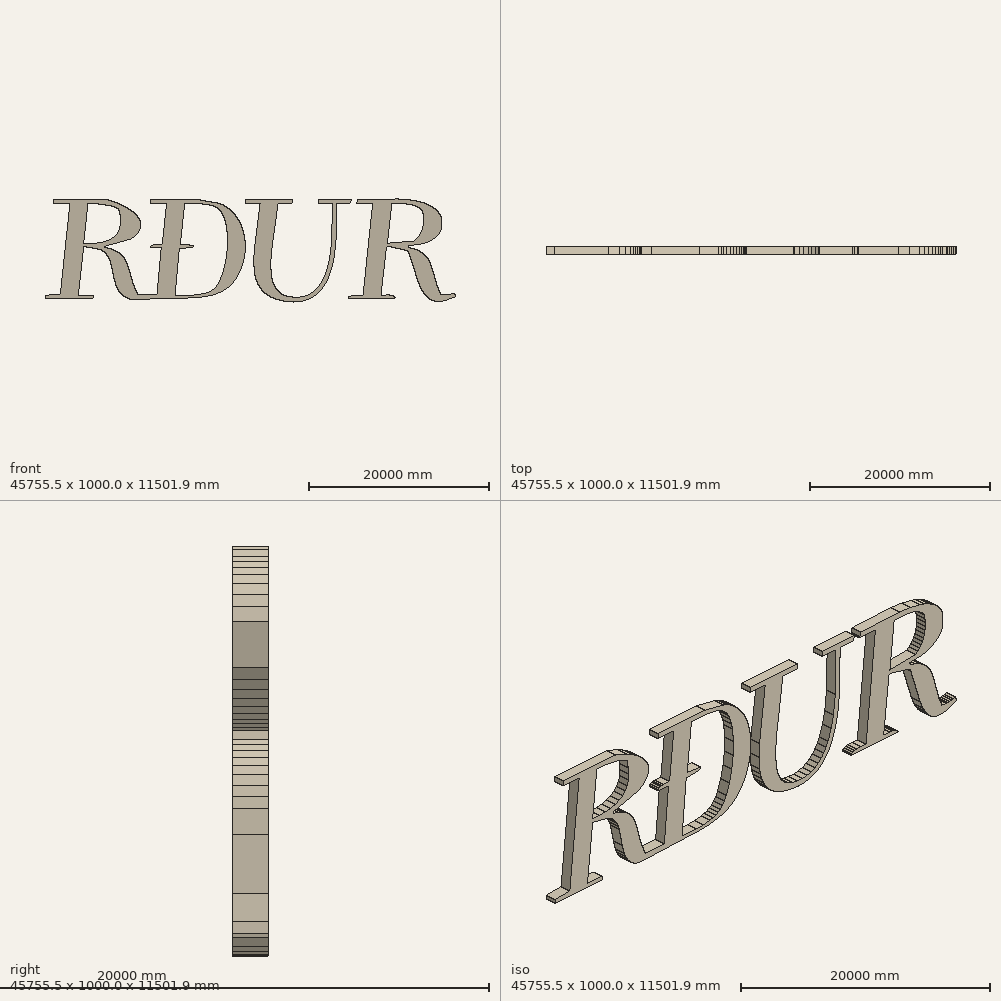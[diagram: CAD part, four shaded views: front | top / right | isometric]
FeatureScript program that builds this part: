
annotation { "Feature Type Name" : "Feature", "Feature Type Description" : "" }
export const myFeature = defineFeature(function(context is Context, id is Id, definition is map)
    precondition{}
    {
        {
            var Q0;
            Q0=qCreatedBy(makeId("Front.planeOp"),FACE);
            var sketch = newSketch(context, id + "F0", { "sketchPlane" : qUnion([Q0])});
            skPoint(sketch, "E0.0", {"position": v(4657, 1520.6) * mm});
            skPoint(sketch, "E1.0", {"position": v(4445.34, -322.18) * mm});
            skPoint(sketch, "E2.0", {"position": v(4195.1, -1476.1) * mm});
            skPoint(sketch, "E3.0", {"position": v(3835.48, -2522.07) * mm});
            skPoint(sketch, "E4.0", {"position": v(4716.46, 5621.12) * mm});
            skPoint(sketch, "E5.0", {"position": v(3175.32, 5621.43) * mm});
            skPoint(sketch, "E6.0", {"position": v(3175.32, 6095.06) * mm});
            skPoint(sketch, "E7.0", {"position": v(6849.4, 6095.06) * mm});
            skPoint(sketch, "E8.0", {"position": v(6730.98, 5621.43) * mm});
            skPoint(sketch, "E9.0", {"position": v(5190.21, 5621.43) * mm});
            skPoint(sketch, "E10.0", {"position": v(5151.27, 1686.8) * mm});
            skPoint(sketch, "E11.0", {"position": v(4941.19, -292.45) * mm});
            skPoint(sketch, "E12.0", {"position": v(4680.2, -1529.03) * mm});
            skPoint(sketch, "E13.0", {"position": v(4297.02, -2654.94) * mm});
            skPoint(sketch, "E14.0", {"position": v(3769.68, -3631.87) * mm});
            skPoint(sketch, "E15.0", {"position": v(3347.68, -3419.16) * mm});
            skPoint(sketch, "E16.0", {"position": v(2712.8, -4125.95) * mm});
            skPoint(sketch, "E17.0", {"position": v(3076.44, -4421.97) * mm});
            skPoint(sketch, "E18.0", {"position": v(3608.8, -2991.86) * mm});
            skPoint(sketch, "E19.0", {"position": v(4052.76, -3164.4) * mm});
            skPoint(sketch, "E20.0", {"position": v(3445.1, -4052.77) * mm});
            skPoint(sketch, "E21.0", {"position": v(3049.7, -3798.86) * mm});
            skPoint(sketch, "E22.0", {"position": v(2660.67, -4735.08) * mm});
            skPoint(sketch, "E23.0", {"position": v(2334.25, -4395.11) * mm});
            skPoint(sketch, "E24.0", {"position": v(1911.9, -4601.1) * mm});
            skPoint(sketch, "E25.0", {"position": v(2195.1, -4987.1) * mm});
            skPoint(sketch, "E26.0", {"position": v(1677.27, -5173.5) * mm});
            skPoint(sketch, "E27.0", {"position": v(1443.39, -4739.05) * mm});
            skPoint(sketch, "E28.0", {"position": v(926.42, -4803.62) * mm});
            skPoint(sketch, "E29.0", {"position": v(1104.03, -5289.22) * mm});
            skPoint(sketch, "E30.0", {"position": v(473.17, -5329.68) * mm});
            skPoint(sketch, "E31.0", {"position": v(358.42, -4789.65) * mm});
            skPoint(sketch, "E32.0", {"position": v(-262.67, -4692.11) * mm});
            skPoint(sketch, "E33.0", {"position": v(-218.6, -5289.95) * mm});
            skPoint(sketch, "E34.0", {"position": v(-973.85, -5165.62) * mm});
            skPoint(sketch, "E35.0", {"position": v(-729.59, -4539.58) * mm});
            skPoint(sketch, "E36.0", {"position": v(-1119, -4307.22) * mm});
            skPoint(sketch, "E37.0", {"position": v(-1602.27, -4992.77) * mm});
            skPoint(sketch, "E38.0", {"position": v(-2144.75, -4764.44) * mm});
            skPoint(sketch, "E39.0", {"position": v(-1436.99, -4002.3) * mm});
            skPoint(sketch, "E40.0", {"position": v(-1688.7, -3631.38) * mm});
            skPoint(sketch, "E41.0", {"position": v(-2606.54, -4484.04) * mm});
            skPoint(sketch, "E42.0", {"position": v(-2993.38, -4154.94) * mm});
            skPoint(sketch, "E43.0", {"position": v(-1880.1, -3201.51) * mm});
            skPoint(sketch, "E44.0", {"position": v(-3310.52, -3780.5) * mm});
            skPoint(sketch, "E45.0", {"position": v(-4054.66, -770.79) * mm});
            skPoint(sketch, "E46.0", {"position": v(-3991.06, -1896.82) * mm});
            skPoint(sketch, "E47.0", {"position": v(-3898.29, -2418.86) * mm});
            skPoint(sketch, "E48.0", {"position": v(-3757.54, -2909.21) * mm});
            skPoint(sketch, "E49.0", {"position": v(-3563.45, -3364.1) * mm});
            skPoint(sketch, "E50.0", {"position": v(-2016.82, -2719.64) * mm});
            skPoint(sketch, "E51.0", {"position": v(-2104.22, -2192.6) * mm});
            skPoint(sketch, "E52.0", {"position": v(-2154.15, -1030.92) * mm});
            skPoint(sketch, "E53.0", {"position": v(-2075.3, 228.42) * mm});
            skPoint(sketch, "E54.0", {"position": v(-3991.92, 442.1) * mm});
            skPoint(sketch, "E55.0", {"position": v(-3344.33, 5621.12) * mm});
            skPoint(sketch, "E56.0", {"position": v(-5003.76, 5621.43) * mm});
            skPoint(sketch, "E57.0", {"position": v(-5003.76, 6095.06) * mm});
            skPoint(sketch, "E58.0", {"position": v(329.86, 6095.06) * mm});
            skPoint(sketch, "E59.0", {"position": v(329.86, 5621.43) * mm});
            skPoint(sketch, "E60.0", {"position": v(-1329.44, 5621.43) * mm});
            skLineSegment(sketch, "E61", {"start": v(-5003.76, 6095.06) * mm, "end": v(329.86, 6095.06) * mm});
            skLineSegment(sketch, "E62", {"start": v(329.86, 6095.06) * mm, "end": v(329.86, 5621.43) * mm});
            skLineSegment(sketch, "E63", {"start": v(329.86, 5621.43) * mm, "end": v(-1329.44, 5621.43) * mm});
            skLineSegment(sketch, "E64", {"start": v(-1329.44, 5621.43) * mm, "end": v(-2075.3, 228.42) * mm});
            skLineSegment(sketch, "E65", {"start": v(-2075.3, 228.42) * mm, "end": v(-2154.15, -1030.92) * mm});
            skLineSegment(sketch, "E66", {"start": v(-2154.15, -1030.92) * mm, "end": v(-2104.22, -2192.6) * mm});
            skLineSegment(sketch, "E67", {"start": v(-2104.22, -2192.6) * mm, "end": v(-2016.82, -2719.64) * mm});
            skLineSegment(sketch, "E68", {"start": v(-2016.82, -2719.64) * mm, "end": v(-1880.1, -3201.51) * mm});
            skLineSegment(sketch, "E69", {"start": v(-1880.1, -3201.51) * mm, "end": v(-1688.7, -3631.38) * mm});
            skLineSegment(sketch, "E70", {"start": v(-1688.7, -3631.38) * mm, "end": v(-1436.99, -4002.3) * mm});
            skLineSegment(sketch, "E71", {"start": v(-1436.99, -4002.3) * mm, "end": v(-1119, -4307.22) * mm});
            skLineSegment(sketch, "E72", {"start": v(-1119, -4307.22) * mm, "end": v(-729.59, -4539.58) * mm});
            skLineSegment(sketch, "E73", {"start": v(-729.59, -4539.58) * mm, "end": v(-262.67, -4692.11) * mm});
            skLineSegment(sketch, "E74", {"start": v(-262.67, -4692.11) * mm, "end": v(358.42, -4789.65) * mm});
            skLineSegment(sketch, "E75", {"start": v(358.42, -4789.65) * mm, "end": v(926.42, -4803.62) * mm});
            skLineSegment(sketch, "E76", {"start": v(926.42, -4803.62) * mm, "end": v(1443.39, -4739.05) * mm});
            skLineSegment(sketch, "E77", {"start": v(1443.39, -4739.05) * mm, "end": v(1911.9, -4601.1) * mm});
            skLineSegment(sketch, "E78", {"start": v(1911.9, -4601.1) * mm, "end": v(2334.25, -4395.11) * mm});
            skLineSegment(sketch, "E79", {"start": v(2334.25, -4395.11) * mm, "end": v(2712.8, -4125.95) * mm});
            skLineSegment(sketch, "E80", {"start": v(2712.8, -4125.95) * mm, "end": v(3049.7, -3798.86) * mm});
            skLineSegment(sketch, "E81", {"start": v(3049.7, -3798.86) * mm, "end": v(3347.68, -3419.16) * mm});
            skLineSegment(sketch, "E82", {"start": v(3347.68, -3419.16) * mm, "end": v(3608.8, -2991.86) * mm});
            skLineSegment(sketch, "E83", {"start": v(3608.8, -2991.86) * mm, "end": v(3835.48, -2522.07) * mm});
            skLineSegment(sketch, "E84", {"start": v(3835.48, -2522.07) * mm, "end": v(4195.1, -1476.1) * mm});
            skLineSegment(sketch, "E85", {"start": v(4195.1, -1476.1) * mm, "end": v(4445.34, -322.18) * mm});
            skLineSegment(sketch, "E86", {"start": v(4445.34, -322.18) * mm, "end": v(4657, 1520.6) * mm});
            skLineSegment(sketch, "E87", {"start": v(4657, 1520.6) * mm, "end": v(4716.46, 5621.12) * mm});
            skLineSegment(sketch, "E88", {"start": v(4716.46, 5621.12) * mm, "end": v(3175.32, 5621.43) * mm});
            skLineSegment(sketch, "E89", {"start": v(3175.32, 5621.43) * mm, "end": v(3175.32, 6095.06) * mm});
            skLineSegment(sketch, "E90", {"start": v(3175.32, 6095.06) * mm, "end": v(6849.4, 6095.06) * mm});
            skLineSegment(sketch, "E91", {"start": v(6849.4, 6095.06) * mm, "end": v(6730.98, 5621.43) * mm});
            skLineSegment(sketch, "E92", {"start": v(6730.98, 5621.43) * mm, "end": v(5190.21, 5621.43) * mm});
            skLineSegment(sketch, "E93", {"start": v(5190.21, 5621.43) * mm, "end": v(5151.27, 1686.8) * mm});
            skLineSegment(sketch, "E94", {"start": v(5151.27, 1686.8) * mm, "end": v(4941.19, -292.45) * mm});
            skLineSegment(sketch, "E95", {"start": v(4941.19, -292.45) * mm, "end": v(4680.2, -1529.03) * mm});
            skLineSegment(sketch, "E96", {"start": v(4680.2, -1529.03) * mm, "end": v(4297.02, -2654.94) * mm});
            skLineSegment(sketch, "E97", {"start": v(4297.02, -2654.94) * mm, "end": v(4052.76, -3164.4) * mm});
            skLineSegment(sketch, "E98", {"start": v(4052.76, -3164.4) * mm, "end": v(3769.68, -3631.87) * mm});
            skLineSegment(sketch, "E99", {"start": v(3769.68, -3631.87) * mm, "end": v(3445.1, -4052.77) * mm});
            skLineSegment(sketch, "E100", {"start": v(3445.1, -4052.77) * mm, "end": v(3076.44, -4421.97) * mm});
            skLineSegment(sketch, "E101", {"start": v(3076.44, -4421.97) * mm, "end": v(2660.67, -4735.08) * mm});
            skLineSegment(sketch, "E102", {"start": v(2660.67, -4735.08) * mm, "end": v(2195.1, -4987.1) * mm});
            skLineSegment(sketch, "E103", {"start": v(2195.1, -4987.1) * mm, "end": v(1677.27, -5173.5) * mm});
            skLineSegment(sketch, "E104", {"start": v(1677.27, -5173.5) * mm, "end": v(1104.03, -5289.22) * mm});
            skLineSegment(sketch, "E105", {"start": v(1104.03, -5289.22) * mm, "end": v(473.17, -5329.68) * mm});
            skLineSegment(sketch, "E106", {"start": v(473.17, -5329.68) * mm, "end": v(-218.6, -5289.95) * mm});
            skLineSegment(sketch, "E107", {"start": v(-218.6, -5289.95) * mm, "end": v(-973.85, -5165.62) * mm});
            skLineSegment(sketch, "E108", {"start": v(-973.85, -5165.62) * mm, "end": v(-1602.27, -4992.77) * mm});
            skLineSegment(sketch, "E109", {"start": v(-1602.27, -4992.77) * mm, "end": v(-2144.75, -4764.44) * mm});
            skLineSegment(sketch, "E110", {"start": v(-2144.75, -4764.44) * mm, "end": v(-2606.54, -4484.04) * mm});
            skLineSegment(sketch, "E111", {"start": v(-2606.54, -4484.04) * mm, "end": v(-2993.38, -4154.94) * mm});
            skLineSegment(sketch, "E112", {"start": v(-2993.38, -4154.94) * mm, "end": v(-3310.52, -3780.5) * mm});
            skLineSegment(sketch, "E113", {"start": v(-3310.52, -3780.5) * mm, "end": v(-3563.45, -3364.1) * mm});
            skLineSegment(sketch, "E114", {"start": v(-3563.45, -3364.1) * mm, "end": v(-3757.54, -2909.21) * mm});
            skLineSegment(sketch, "E115", {"start": v(-3757.54, -2909.21) * mm, "end": v(-3898.29, -2418.86) * mm});
            skLineSegment(sketch, "E116", {"start": v(-3898.29, -2418.86) * mm, "end": v(-3991.06, -1896.82) * mm});
            skLineSegment(sketch, "E117", {"start": v(-3991.06, -1896.82) * mm, "end": v(-4054.66, -770.79) * mm});
            skLineSegment(sketch, "E118", {"start": v(-4054.66, -770.79) * mm, "end": v(-3991.92, 442.1) * mm});
            skLineSegment(sketch, "E119", {"start": v(-3991.92, 442.1) * mm, "end": v(-3344.33, 5621.12) * mm});
            skLineSegment(sketch, "E120", {"start": v(-3344.33, 5621.12) * mm, "end": v(-5003.76, 5621.43) * mm});
            skLineSegment(sketch, "E121", {"start": v(-5003.76, 6095.06) * mm, "end": v(-5003.76, 5621.43) * mm});
            skPoint(sketch, "E122.0", {"position": v(7442.78, 5739.53) * mm});
            skPoint(sketch, "E123.0", {"position": v(7442.78, 5621.43) * mm});
            skPoint(sketch, "E124.0", {"position": v(7561.18, 6095.06) * mm});
            skPoint(sketch, "E125.0", {"position": v(9220.85, 5621.12) * mm});
            skPoint(sketch, "E126.0", {"position": v(12006.25, 6172.2) * mm});
            skPoint(sketch, "E127.0", {"position": v(13216.46, 6086.94) * mm});
            skPoint(sketch, "E128.0", {"position": v(14330.6, 5902.98) * mm});
            skPoint(sketch, "E129.0", {"position": v(14839.75, 5765.29) * mm});
            skPoint(sketch, "E130.0", {"position": v(15310.7, 5592.43) * mm});
            skPoint(sketch, "E131.0", {"position": v(15738.55, 5381.13) * mm});
            skPoint(sketch, "E132.0", {"position": v(16118.68, 5127.71) * mm});
            skPoint(sketch, "E133.0", {"position": v(16446.32, 4828.7) * mm});
            skPoint(sketch, "E134.0", {"position": v(16716.82, 4480.56) * mm});
            skPoint(sketch, "E135.0", {"position": v(16925.32, 4080.04) * mm});
            skPoint(sketch, "E136.0", {"position": v(16925.32, 2776.27) * mm});
            skPoint(sketch, "E137.0", {"position": v(16763.33, 2447.1) * mm});
            skPoint(sketch, "E138.0", {"position": v(16554.71, 2154.26) * mm});
            skPoint(sketch, "E139.0", {"position": v(16303.25, 1896.88) * mm});
            skPoint(sketch, "E140.0", {"position": v(16011.62, 1673.67) * mm});
            skPoint(sketch, "E141.0", {"position": v(15683.62, 1484.1) * mm});
            skPoint(sketch, "E142.0", {"position": v(15322.17, 1327.18) * mm});
            skPoint(sketch, "E143.0", {"position": v(14930.93, 1201.8) * mm});
            skPoint(sketch, "E144.0", {"position": v(14512.97, 1107.2) * mm});
            skPoint(sketch, "E145.0", {"position": v(13610.38, 1006.5) * mm});
            skPoint(sketch, "E146.0", {"position": v(13132.35, 998.5) * mm});
            skPoint(sketch, "E147.0", {"position": v(13250.64, 761.01) * mm});
            skPoint(sketch, "E148.0", {"position": v(13779.08, 629.24) * mm});
            skPoint(sketch, "E149.0", {"position": v(14228.18, 461.88) * mm});
            skPoint(sketch, "E150.0", {"position": v(14606.1, 260.83) * mm});
            skPoint(sketch, "E151.0", {"position": v(14921.53, 28.04) * mm});
            skPoint(sketch, "E152.0", {"position": v(15182.52, -233.98) * mm});
            skPoint(sketch, "E153.0", {"position": v(15396.88, -523.6) * mm});
            skPoint(sketch, "E154.0", {"position": v(15573.51, -838.23) * mm});
            skPoint(sketch, "E155.0", {"position": v(15720.12, -1176.12) * mm});
            skPoint(sketch, "E156.0", {"position": v(15956.94, -1912.5) * mm});
            skPoint(sketch, "E157.0", {"position": v(16434.47, -3568.94) * mm});
            skPoint(sketch, "E158.0", {"position": v(16806.79, -4454.75) * mm});
            skPoint(sketch, "E159.0", {"position": v(17299.95, -4508.27) * mm});
            skPoint(sketch, "E160.0", {"position": v(17516.26, -4511.81) * mm});
            skPoint(sketch, "E161.0", {"position": v(17721.7, -4497.84) * mm});
            skPoint(sketch, "E162.0", {"position": v(17924.1, -4465) * mm});
            skPoint(sketch, "E163.0", {"position": v(18130.64, -4411.66) * mm});
            skPoint(sketch, "E164.0", {"position": v(18347.8, -4336.58) * mm});
            skPoint(sketch, "E165.0", {"position": v(18466.33, -4691.93) * mm});
            skPoint(sketch, "E166.0", {"position": v(18466.33, -4809.97) * mm});
            skPoint(sketch, "E167.0", {"position": v(18229.52, -4809.97) * mm});
            skPoint(sketch, "E168.0", {"position": v(17725.61, -5041.3) * mm});
            skPoint(sketch, "E169.0", {"position": v(17265.04, -5192.66) * mm});
            skPoint(sketch, "E170.0", {"position": v(16844.87, -5269.5) * mm});
            skPoint(sketch, "E171.0", {"position": v(16462.8, -5277.38) * mm});
            skPoint(sketch, "E172.0", {"position": v(16116.36, -5221.84) * mm});
            skPoint(sketch, "E173.0", {"position": v(15802.88, -5108.07) * mm});
            skPoint(sketch, "E174.0", {"position": v(15520.05, -4941.87) * mm});
            skPoint(sketch, "E175.0", {"position": v(15265.16, -4728.55) * mm});
            skPoint(sketch, "E176.0", {"position": v(15035.91, -4473.54) * mm});
            skPoint(sketch, "E177.0", {"position": v(14830.23, -4182.35) * mm});
            skPoint(sketch, "E178.0", {"position": v(14644.92, -3860.5) * mm});
            skPoint(sketch, "E179.0", {"position": v(14326.32, -3146.58) * mm});
            skPoint(sketch, "E180.0", {"position": v(13262.97, 141.93) * mm});
            skPoint(sketch, "E181.0", {"position": v(13132.72, 405.48) * mm});
            skPoint(sketch, "E182.0", {"position": v(10998.8, 879.97) * mm});
            skPoint(sketch, "E183.0", {"position": v(10761.5, 761.44) * mm});
            skPoint(sketch, "E184.0", {"position": v(10168.48, -4454.56) * mm});
            skPoint(sketch, "E185.0", {"position": v(10287.26, -4573.4) * mm});
            skPoint(sketch, "E186.0", {"position": v(10867.58, -4537.08) * mm});
            skPoint(sketch, "E187.0", {"position": v(11118.8, -4542.45) * mm});
            skPoint(sketch, "E188.0", {"position": v(11341.95, -4575.41) * mm});
            skPoint(sketch, "E189.0", {"position": v(11535.67, -4644.87) * mm});
            skPoint(sketch, "E190.0", {"position": v(11698.02, -4759.62) * mm});
            skPoint(sketch, "E191.0", {"position": v(11827.66, -4928.56) * mm});
            skPoint(sketch, "E192.0", {"position": v(6494.41, -4928.56) * mm});
            skPoint(sketch, "E193.0", {"position": v(6494.41, -4810.58) * mm});
            skPoint(sketch, "E194.0", {"position": v(6659.7, -4710.12) * mm});
            skPoint(sketch, "E195.0", {"position": v(6856.96, -4639.32) * mm});
            skPoint(sketch, "E196.0", {"position": v(7081.32, -4593.66) * mm});
            skPoint(sketch, "E197.0", {"position": v(7592.07, -4559.85) * mm});
            skPoint(sketch, "E198.0", {"position": v(8153.71, -4573.46) * mm});
            skLineSegment(sketch, "E199", {"start": v(16925.32, 4080.04) * mm, "end": v(16925.32, 2776.27) * mm});
            skLineSegment(sketch, "E200", {"start": v(16925.32, 2776.27) * mm, "end": v(16763.33, 2447.1) * mm});
            skLineSegment(sketch, "E201", {"start": v(16763.33, 2447.1) * mm, "end": v(16554.71, 2154.26) * mm});
            skLineSegment(sketch, "E202", {"start": v(16554.71, 2154.26) * mm, "end": v(16303.25, 1896.88) * mm});
            skLineSegment(sketch, "E203", {"start": v(16303.25, 1896.88) * mm, "end": v(16011.62, 1673.67) * mm});
            skLineSegment(sketch, "E204", {"start": v(16011.62, 1673.67) * mm, "end": v(15683.62, 1484.1) * mm});
            skLineSegment(sketch, "E205", {"start": v(15683.62, 1484.1) * mm, "end": v(15322.17, 1327.18) * mm});
            skLineSegment(sketch, "E206", {"start": v(15322.17, 1327.18) * mm, "end": v(14930.93, 1201.8) * mm});
            skLineSegment(sketch, "E207", {"start": v(14930.93, 1201.8) * mm, "end": v(14512.97, 1107.2) * mm});
            skLineSegment(sketch, "E208", {"start": v(14512.97, 1107.2) * mm, "end": v(13610.38, 1006.5) * mm});
            skLineSegment(sketch, "E209", {"start": v(13610.38, 1006.5) * mm, "end": v(13132.35, 998.5) * mm});
            skLineSegment(sketch, "E210", {"start": v(13132.35, 998.5) * mm, "end": v(13250.64, 761.01) * mm});
            skLineSegment(sketch, "E211", {"start": v(13250.64, 761.01) * mm, "end": v(13779.08, 629.24) * mm});
            skLineSegment(sketch, "E212", {"start": v(13779.08, 629.24) * mm, "end": v(14228.18, 461.88) * mm});
            skLineSegment(sketch, "E213", {"start": v(14228.18, 461.88) * mm, "end": v(14606.1, 260.83) * mm});
            skLineSegment(sketch, "E214", {"start": v(14606.1, 260.83) * mm, "end": v(14921.53, 28.04) * mm});
            skLineSegment(sketch, "E215", {"start": v(14921.53, 28.04) * mm, "end": v(15182.52, -233.98) * mm});
            skLineSegment(sketch, "E216", {"start": v(15396.88, -523.6) * mm, "end": v(15182.52, -233.98) * mm});
            skLineSegment(sketch, "E217", {"start": v(15396.88, -523.6) * mm, "end": v(15573.51, -838.23) * mm});
            skLineSegment(sketch, "E218", {"start": v(15573.51, -838.23) * mm, "end": v(15720.12, -1176.12) * mm});
            skLineSegment(sketch, "E219", {"start": v(15720.12, -1176.12) * mm, "end": v(15956.94, -1912.5) * mm});
            skLineSegment(sketch, "E220", {"start": v(15956.94, -1912.5) * mm, "end": v(16434.47, -3568.94) * mm});
            skLineSegment(sketch, "E221", {"start": v(16434.47, -3568.94) * mm, "end": v(16806.79, -4454.75) * mm});
            skLineSegment(sketch, "E222", {"start": v(16806.79, -4454.75) * mm, "end": v(17299.95, -4508.27) * mm});
            skLineSegment(sketch, "E223", {"start": v(17299.95, -4508.27) * mm, "end": v(17516.26, -4511.81) * mm});
            skLineSegment(sketch, "E224", {"start": v(17516.26, -4511.81) * mm, "end": v(17721.7, -4497.84) * mm});
            skLineSegment(sketch, "E225", {"start": v(17721.7, -4497.84) * mm, "end": v(17924.1, -4465) * mm});
            skLineSegment(sketch, "E226", {"start": v(17924.1, -4465) * mm, "end": v(18130.64, -4411.66) * mm});
            skLineSegment(sketch, "E227", {"start": v(18130.64, -4411.66) * mm, "end": v(18347.8, -4336.58) * mm});
            skLineSegment(sketch, "E228", {"start": v(18347.8, -4336.58) * mm, "end": v(18466.33, -4691.93) * mm});
            skLineSegment(sketch, "E229", {"start": v(18466.33, -4691.93) * mm, "end": v(18466.33, -4809.97) * mm});
            skLineSegment(sketch, "E230", {"start": v(18466.33, -4809.97) * mm, "end": v(18229.52, -4809.97) * mm});
            skLineSegment(sketch, "E231", {"start": v(18229.52, -4809.97) * mm, "end": v(17725.61, -5041.3) * mm});
            skLineSegment(sketch, "E232", {"start": v(17725.61, -5041.3) * mm, "end": v(17265.04, -5192.66) * mm});
            skLineSegment(sketch, "E233", {"start": v(17265.04, -5192.66) * mm, "end": v(16844.87, -5269.5) * mm});
            skLineSegment(sketch, "E234", {"start": v(16844.87, -5269.5) * mm, "end": v(16462.8, -5277.38) * mm});
            skLineSegment(sketch, "E235", {"start": v(16462.8, -5277.38) * mm, "end": v(16116.36, -5221.84) * mm});
            skLineSegment(sketch, "E236", {"start": v(16116.36, -5221.84) * mm, "end": v(15802.88, -5108.07) * mm});
            skLineSegment(sketch, "E237", {"start": v(15802.88, -5108.07) * mm, "end": v(15520.05, -4941.87) * mm});
            skLineSegment(sketch, "E238", {"start": v(15520.05, -4941.87) * mm, "end": v(15265.16, -4728.55) * mm});
            skLineSegment(sketch, "E239", {"start": v(15265.16, -4728.55) * mm, "end": v(15035.91, -4473.54) * mm});
            skLineSegment(sketch, "E240", {"start": v(15035.91, -4473.54) * mm, "end": v(14830.23, -4182.35) * mm});
            skLineSegment(sketch, "E241", {"start": v(14830.23, -4182.35) * mm, "end": v(14644.92, -3860.5) * mm});
            skLineSegment(sketch, "E242", {"start": v(14644.92, -3860.5) * mm, "end": v(14326.32, -3146.58) * mm});
            skLineSegment(sketch, "E243", {"start": v(14326.32, -3146.58) * mm, "end": v(13262.97, 141.93) * mm});
            skLineSegment(sketch, "E244", {"start": v(13262.97, 141.93) * mm, "end": v(13132.72, 405.48) * mm});
            skLineSegment(sketch, "E245", {"start": v(13132.72, 405.48) * mm, "end": v(10998.8, 879.97) * mm});
            skLineSegment(sketch, "E246", {"start": v(10998.8, 879.97) * mm, "end": v(10761.5, 761.44) * mm});
            skLineSegment(sketch, "E247", {"start": v(10761.5, 761.44) * mm, "end": v(10168.48, -4454.56) * mm});
            skLineSegment(sketch, "E248", {"start": v(16925.32, 4080.04) * mm, "end": v(16716.82, 4480.56) * mm});
            skLineSegment(sketch, "E249", {"start": v(16716.82, 4480.56) * mm, "end": v(16446.32, 4828.7) * mm});
            skLineSegment(sketch, "E250", {"start": v(16446.32, 4828.7) * mm, "end": v(16118.68, 5127.71) * mm});
            skLineSegment(sketch, "E251", {"start": v(16118.68, 5127.71) * mm, "end": v(15738.55, 5381.13) * mm});
            skLineSegment(sketch, "E252", {"start": v(15738.55, 5381.13) * mm, "end": v(15310.7, 5592.43) * mm});
            skLineSegment(sketch, "E253", {"start": v(15310.7, 5592.43) * mm, "end": v(14839.75, 5765.29) * mm});
            skLineSegment(sketch, "E254", {"start": v(14839.75, 5765.29) * mm, "end": v(14330.6, 5902.98) * mm});
            skLineSegment(sketch, "E255", {"start": v(14330.6, 5902.98) * mm, "end": v(13216.46, 6086.94) * mm});
            skLineSegment(sketch, "E256", {"start": v(13216.46, 6086.94) * mm, "end": v(12006.25, 6172.2) * mm});
            skLineSegment(sketch, "E257", {"start": v(12006.25, 6172.2) * mm, "end": v(7561.18, 6095.06) * mm});
            skLineSegment(sketch, "E258", {"start": v(7561.18, 6095.06) * mm, "end": v(7442.78, 5739.53) * mm});
            skLineSegment(sketch, "E259", {"start": v(7442.78, 5739.53) * mm, "end": v(7442.78, 5621.43) * mm});
            skLineSegment(sketch, "E260", {"start": v(7442.78, 5621.43) * mm, "end": v(9220.85, 5621.12) * mm});
            skLineSegment(sketch, "E261", {"start": v(9220.85, 5621.12) * mm, "end": v(8153.71, -4573.46) * mm});
            skLineSegment(sketch, "E262", {"start": v(8153.71, -4573.46) * mm, "end": v(7592.07, -4559.85) * mm});
            skLineSegment(sketch, "E263", {"start": v(7592.07, -4559.85) * mm, "end": v(7081.32, -4593.66) * mm});
            skLineSegment(sketch, "E264", {"start": v(7081.32, -4593.66) * mm, "end": v(6856.96, -4639.32) * mm});
            skLineSegment(sketch, "E265", {"start": v(6856.96, -4639.32) * mm, "end": v(6659.7, -4710.12) * mm});
            skLineSegment(sketch, "E266", {"start": v(6659.7, -4710.12) * mm, "end": v(6494.41, -4810.58) * mm});
            skLineSegment(sketch, "E267", {"start": v(6494.41, -4810.58) * mm, "end": v(6494.41, -4928.56) * mm});
            skLineSegment(sketch, "E268", {"start": v(6494.41, -4928.56) * mm, "end": v(11827.66, -4928.56) * mm});
            skLineSegment(sketch, "E269", {"start": v(11827.66, -4928.56) * mm, "end": v(11698.02, -4759.62) * mm});
            skLineSegment(sketch, "E270", {"start": v(11698.02, -4759.62) * mm, "end": v(11535.67, -4644.87) * mm});
            skLineSegment(sketch, "E271", {"start": v(11535.67, -4644.87) * mm, "end": v(11341.95, -4575.41) * mm});
            skLineSegment(sketch, "E272", {"start": v(11341.95, -4575.41) * mm, "end": v(11118.8, -4542.45) * mm});
            skLineSegment(sketch, "E273", {"start": v(11118.8, -4542.45) * mm, "end": v(10867.58, -4537.08) * mm});
            skLineSegment(sketch, "E274", {"start": v(10867.58, -4537.08) * mm, "end": v(10287.26, -4573.4) * mm});
            skLineSegment(sketch, "E275", {"start": v(10287.26, -4573.4) * mm, "end": v(10168.48, -4454.56) * mm});
            skPoint(sketch, "E276.0", {"position": v(11354.27, 5621.43) * mm});
            skPoint(sketch, "E277.0", {"position": v(12575.7, 5641.2) * mm});
            skPoint(sketch, "E278.0", {"position": v(13272.24, 5588.28) * mm});
            skPoint(sketch, "E279.0", {"position": v(13584.99, 5530.97) * mm});
            skPoint(sketch, "E280.0", {"position": v(13873.8, 5448.4) * mm});
            skPoint(sketch, "E281.0", {"position": v(14139.19, 5336.82) * mm});
            skPoint(sketch, "E282.0", {"position": v(14380.64, 5192.71) * mm});
            skPoint(sketch, "E283.0", {"position": v(14598.41, 5011.93) * mm});
            skPoint(sketch, "E284.0", {"position": v(14792.26, 4791.47) * mm});
            skPoint(sketch, "E285.0", {"position": v(14865.26, 4390.29) * mm});
            skPoint(sketch, "E286.0", {"position": v(14903.6, 4006.07) * mm});
            skPoint(sketch, "E287.0", {"position": v(14908.1, 3639.5) * mm});
            skPoint(sketch, "E288.0", {"position": v(14879.66, 3291.78) * mm});
            skPoint(sketch, "E289.0", {"position": v(14819.48, 2963.83) * mm});
            skPoint(sketch, "E290.0", {"position": v(14728.42, 2656.77) * mm});
            skPoint(sketch, "E291.0", {"position": v(14607.33, 2371.73) * mm});
            skPoint(sketch, "E292.0", {"position": v(14457.42, 2109.7) * mm});
            skPoint(sketch, "E293.0", {"position": v(14279.45, 1871.8) * mm});
            skPoint(sketch, "E294.0", {"position": v(14074.61, 1658.84) * mm});
            skPoint(sketch, "E295.0", {"position": v(13843.53, 1471.89) * mm});
            skPoint(sketch, "E296.0", {"position": v(10879.66, 1235.2) * mm});
            skLineSegment(sketch, "E297", {"start": v(11354.27, 5621.43) * mm, "end": v(10879.66, 1235.2) * mm});
            skLineSegment(sketch, "E298", {"start": v(10879.66, 1235.2) * mm, "end": v(13843.53, 1471.89) * mm});
            skLineSegment(sketch, "E299", {"start": v(13843.53, 1471.89) * mm, "end": v(14074.61, 1658.84) * mm});
            skLineSegment(sketch, "E300", {"start": v(14074.61, 1658.84) * mm, "end": v(14279.45, 1871.8) * mm});
            skLineSegment(sketch, "E301", {"start": v(14279.45, 1871.8) * mm, "end": v(14457.42, 2109.7) * mm});
            skLineSegment(sketch, "E302", {"start": v(14457.42, 2109.7) * mm, "end": v(14607.33, 2371.73) * mm});
            skLineSegment(sketch, "E303", {"start": v(14607.33, 2371.73) * mm, "end": v(14728.42, 2656.77) * mm});
            skLineSegment(sketch, "E304", {"start": v(14728.42, 2656.77) * mm, "end": v(14819.48, 2963.83) * mm});
            skLineSegment(sketch, "E305", {"start": v(14819.48, 2963.83) * mm, "end": v(14879.66, 3291.78) * mm});
            skLineSegment(sketch, "E306", {"start": v(14879.66, 3291.78) * mm, "end": v(14908.1, 3639.5) * mm});
            skLineSegment(sketch, "E307", {"start": v(14908.1, 3639.5) * mm, "end": v(14903.6, 4006.07) * mm});
            skLineSegment(sketch, "E308", {"start": v(14903.6, 4006.07) * mm, "end": v(14865.26, 4390.29) * mm});
            skLineSegment(sketch, "E309", {"start": v(14865.26, 4390.29) * mm, "end": v(14792.26, 4791.47) * mm});
            skLineSegment(sketch, "E310", {"start": v(14792.26, 4791.47) * mm, "end": v(14598.41, 5011.93) * mm});
            skLineSegment(sketch, "E311", {"start": v(14598.41, 5011.93) * mm, "end": v(14380.64, 5192.71) * mm});
            skLineSegment(sketch, "E312", {"start": v(14380.64, 5192.71) * mm, "end": v(14139.19, 5336.82) * mm});
            skLineSegment(sketch, "E313", {"start": v(14139.19, 5336.82) * mm, "end": v(13873.8, 5448.4) * mm});
            skLineSegment(sketch, "E314", {"start": v(13873.8, 5448.4) * mm, "end": v(13584.99, 5530.97) * mm});
            skLineSegment(sketch, "E315", {"start": v(13584.99, 5530.97) * mm, "end": v(13272.24, 5588.28) * mm});
            skLineSegment(sketch, "E316", {"start": v(13272.24, 5588.28) * mm, "end": v(12575.7, 5641.2) * mm});
            skLineSegment(sketch, "E317", {"start": v(12575.7, 5641.2) * mm, "end": v(11354.27, 5621.43) * mm});
            skPoint(sketch, "E318.0", {"position": v(-15553.8, 6095.06) * mm});
            skPoint(sketch, "E319.0", {"position": v(-10219.82, 6095.06) * mm});
            skPoint(sketch, "E320.0", {"position": v(-8047.22, 5704.98) * mm});
            skPoint(sketch, "E321.0", {"position": v(-7770.12, 5621.55) * mm});
            skPoint(sketch, "E322.0", {"position": v(-7505.96, 5516.14) * mm});
            skPoint(sketch, "E323.0", {"position": v(-7256.57, 5383.75) * mm});
            skPoint(sketch, "E324.0", {"position": v(-6807.35, 5067.35) * mm});
            skPoint(sketch, "E325.0", {"position": v(-6407.69, 4700.53) * mm});
            skPoint(sketch, "E326.0", {"position": v(-6057.35, 4288.66) * mm});
            skPoint(sketch, "E327.0", {"position": v(-5756.32, 3837.12) * mm});
            skPoint(sketch, "E328.0", {"position": v(-5504.61, 3351.65) * mm});
            skPoint(sketch, "E329.0", {"position": v(-5302.1, 2837.37) * mm});
            skPoint(sketch, "E330.0", {"position": v(-5148.78, 2299.95) * mm});
            skPoint(sketch, "E331.0", {"position": v(-5044.65, 1744.6) * mm});
            skPoint(sketch, "E332.0", {"position": v(-4989.48, 1177.27) * mm});
            skPoint(sketch, "E333.0", {"position": v(-6968.97, 1878.93) * mm});
            skPoint(sketch, "E334.0", {"position": v(-7080.17, 3067.29) * mm});
            skPoint(sketch, "E335.0", {"position": v(-7194.07, 3605.74) * mm});
            skPoint(sketch, "E336.0", {"position": v(-7349.46, 4093.29) * mm});
            skPoint(sketch, "E337.0", {"position": v(-7548.44, 4519.74) * mm});
            skPoint(sketch, "E338.0", {"position": v(-7793.43, 4874.42) * mm});
            skPoint(sketch, "E339.0", {"position": v(-8085.91, 5147.37) * mm});
            skPoint(sketch, "E340.0", {"position": v(-8316.5, 5286.16) * mm});
            skPoint(sketch, "E341.0", {"position": v(-8580.3, 5397.85) * mm});
            skPoint(sketch, "E342.0", {"position": v(-8872.65, 5485.01) * mm});
            skPoint(sketch, "E343.0", {"position": v(-9527.68, 5596.83) * mm});
            skPoint(sketch, "E344.0", {"position": v(-10249.24, 5642.54) * mm});
            skPoint(sketch, "E345.0", {"position": v(-11760.96, 5621.43) * mm});
            skPoint(sketch, "E346.0", {"position": v(-6999.12, 611.11) * mm});
            skPoint(sketch, "E347.0", {"position": v(-7154.27, -653.66) * mm});
            skPoint(sketch, "E348.0", {"position": v(-4983.37, 602.87) * mm});
            skPoint(sketch, "E349.0", {"position": v(-5026.34, 27.19) * mm});
            skPoint(sketch, "E350.0", {"position": v(-5118.02, -544.53) * mm});
            skPoint(sketch, "E351.0", {"position": v(-5258.64, -1106.54) * mm});
            skPoint(sketch, "E352.0", {"position": v(-5447.97, -1653.6) * mm});
            skPoint(sketch, "E353.0", {"position": v(-5686.13, -2180.2) * mm});
            skPoint(sketch, "E354.0", {"position": v(-5973, -2681.06) * mm});
            skPoint(sketch, "E355.0", {"position": v(-7772.8, -2843.3) * mm});
            skPoint(sketch, "E356.0", {"position": v(-7417.7, -1832.74) * mm});
            skPoint(sketch, "E357.0", {"position": v(-6308.45, -3150.49) * mm});
            skPoint(sketch, "E358.0", {"position": v(-6604.1, -3478.43) * mm});
            skPoint(sketch, "E359.0", {"position": v(-6932.1, -3763.64) * mm});
            skPoint(sketch, "E360.0", {"position": v(-7291.23, -4008.58) * mm});
            skPoint(sketch, "E361.0", {"position": v(-7979.71, -3259.56) * mm});
            skPoint(sketch, "E362.0", {"position": v(-8203.34, -3602.57) * mm});
            skPoint(sketch, "E363.0", {"position": v(-8441.62, -3862.34) * mm});
            skPoint(sketch, "E364.0", {"position": v(-7680.03, -4216.83) * mm});
            skPoint(sketch, "E365.0", {"position": v(-8677.22, -4035.25) * mm});
            skPoint(sketch, "E366.0", {"position": v(-8951.63, -4179.9) * mm});
            skPoint(sketch, "E367.0", {"position": v(-9260.35, -4298.56) * mm});
            skPoint(sketch, "E368.0", {"position": v(-9598.85, -4393.53) * mm});
            skPoint(sketch, "E369.0", {"position": v(-9502.05, -4740.33) * mm});
            skPoint(sketch, "E370.0", {"position": v(-8540.38, -4534.46) * mm});
            skPoint(sketch, "E371.0", {"position": v(-8096.65, -4391.09) * mm});
            skPoint(sketch, "E372.0", {"position": v(-10553.32, -4858.68) * mm});
            skPoint(sketch, "E373.0", {"position": v(-10346.78, -4521.21) * mm});
            skPoint(sketch, "E374.0", {"position": v(-11158.54, -4581.58) * mm});
            skPoint(sketch, "E375.0", {"position": v(-12828.1, -4573.15) * mm});
            skPoint(sketch, "E376.0", {"position": v(-14843, -4455) * mm});
            skPoint(sketch, "E377.0", {"position": v(-12353.49, 642.79) * mm});
            skPoint(sketch, "E378.0", {"position": v(-10812.72, 761.44) * mm});
            skPoint(sketch, "E379.0", {"position": v(-10694.55, 997.83) * mm});
            skPoint(sketch, "E380.0", {"position": v(-12235.45, 1116.67) * mm});
            skPoint(sketch, "E381.0", {"position": v(-14250.22, 1116.36) * mm});
            skPoint(sketch, "E382.0", {"position": v(-14922.34, 1107.2) * mm});
            skPoint(sketch, "E383.0", {"position": v(-15104.47, 1079.98) * mm});
            skPoint(sketch, "E384.0", {"position": v(-15269.02, 1035.3) * mm});
            skPoint(sketch, "E385.0", {"position": v(-15418.19, 969.45) * mm});
            skPoint(sketch, "E386.0", {"position": v(-15553.8, 879.42) * mm});
            skPoint(sketch, "E387.0", {"position": v(-15553.8, 761.44) * mm});
            skPoint(sketch, "E388.0", {"position": v(-14368.38, 761.07) * mm});
            skPoint(sketch, "E389.0", {"position": v(-13775.73, 5621.12) * mm});
            skPoint(sketch, "E390.0", {"position": v(-15553.8, 5621.43) * mm});
            skPoint(sketch, "E391.0", {"position": v(-16976.9, -4454.75) * mm});
            skPoint(sketch, "E392.0", {"position": v(-17197.36, -4046.24) * mm});
            skPoint(sketch, "E393.0", {"position": v(-17527.2, -3237.46) * mm});
            skPoint(sketch, "E394.0", {"position": v(-17961.52, -1712.8) * mm});
            skPoint(sketch, "E395.0", {"position": v(-18191.14, -1031.1) * mm});
            skPoint(sketch, "E396.0", {"position": v(-18336.4, -718) * mm});
            skPoint(sketch, "E397.0", {"position": v(-18512.43, -425.88) * mm});
            skPoint(sketch, "E398.0", {"position": v(-18726.9, -157.26) * mm});
            skPoint(sketch, "E399.0", {"position": v(-18987.77, 85.78) * mm});
            skPoint(sketch, "E400.0", {"position": v(-19302.83, 301.3) * mm});
            skPoint(sketch, "E401.0", {"position": v(-19679.9, 487.03) * mm});
            skPoint(sketch, "E402.0", {"position": v(-20126.8, 640.84) * mm});
            skPoint(sketch, "E403.0", {"position": v(-20651.59, 761.07) * mm});
            skPoint(sketch, "E404.0", {"position": v(-20513.65, 28.77) * mm});
            skPoint(sketch, "E405.0", {"position": v(-20298.56, -285.07) * mm});
            skPoint(sketch, "E406.0", {"position": v(-20130.83, -633.15) * mm});
            skPoint(sketch, "E407.0", {"position": v(-20000.1, -1008.7) * mm});
            skPoint(sketch, "E408.0", {"position": v(-19648.78, -2641.33) * mm});
            skPoint(sketch, "E409.0", {"position": v(-19435.76, -3435.95) * mm});
            skPoint(sketch, "E410.0", {"position": v(-19285, -3802.7) * mm});
            skPoint(sketch, "E411.0", {"position": v(-19091.28, -4139.8) * mm});
            skPoint(sketch, "E412.0", {"position": v(-18844.94, -4439.91) * mm});
            skPoint(sketch, "E413.0", {"position": v(-18535.37, -4695.83) * mm});
            skPoint(sketch, "E414.0", {"position": v(-18153.05, -4900.6) * mm});
            skPoint(sketch, "E415.0", {"position": v(-17687.84, -5047.1) * mm});
            skPoint(sketch, "E416.0", {"position": v(-20785.86, 300.87) * mm});
            skPoint(sketch, "E417.0", {"position": v(-21125.22, 524.26) * mm});
            skPoint(sketch, "E418.0", {"position": v(-20651.34, 879.97) * mm});
            skPoint(sketch, "E419.0", {"position": v(-17687.96, 1709.62) * mm});
            skPoint(sketch, "E420.0", {"position": v(-17322.85, 1989.16) * mm});
            skPoint(sketch, "E421.0", {"position": v(-17040.38, 2267.6) * mm});
            skPoint(sketch, "E422.0", {"position": v(-16835.42, 2544.4) * mm});
            skPoint(sketch, "E423.0", {"position": v(-16702.73, 2818.5) * mm});
            skPoint(sketch, "E424.0", {"position": v(-16636.94, 3088.65) * mm});
            skPoint(sketch, "E425.0", {"position": v(-16633.03, 3354.21) * mm});
            skPoint(sketch, "E426.0", {"position": v(-16685.52, 3613.98) * mm});
            skPoint(sketch, "E427.0", {"position": v(-16789.16, 3867.03) * mm});
            skPoint(sketch, "E428.0", {"position": v(-16938.94, 4112.4) * mm});
            skPoint(sketch, "E429.0", {"position": v(-17129.25, 4349.09) * mm});
            skPoint(sketch, "E430.0", {"position": v(-17355.32, 4576.14) * mm});
            skPoint(sketch, "E431.0", {"position": v(-17611.67, 4792.39) * mm});
            skPoint(sketch, "E432.0", {"position": v(-17892.92, 4997.04) * mm});
            skPoint(sketch, "E433.0", {"position": v(-18509.5, 5367.34) * mm});
            skPoint(sketch, "E434.0", {"position": v(-18962.25, 4326.87) * mm});
            skPoint(sketch, "E435.0", {"position": v(-18908.18, 3704.74) * mm});
            skPoint(sketch, "E436.0", {"position": v(-18945.53, 3159.27) * mm});
            skPoint(sketch, "E437.0", {"position": v(-19109.96, 5028.6) * mm});
            skPoint(sketch, "E438.0", {"position": v(-19344.58, 5169.34) * mm});
            skPoint(sketch, "E439.0", {"position": v(-19592.01, 5287.44) * mm});
            skPoint(sketch, "E440.0", {"position": v(-19853, 5384.85) * mm});
            skPoint(sketch, "E441.0", {"position": v(-19163.3, 5678.92) * mm});
            skPoint(sketch, "E442.0", {"position": v(-19071.87, 2687.59) * mm});
            skPoint(sketch, "E443.0", {"position": v(-19285.25, 2287.01) * mm});
            skPoint(sketch, "E444.0", {"position": v(-19583.23, 1954.56) * mm});
            skPoint(sketch, "E445.0", {"position": v(-19963.6, 1687.65) * mm});
            skPoint(sketch, "E446.0", {"position": v(-20423.92, 1483.24) * mm});
            skPoint(sketch, "E447.0", {"position": v(-20962.38, 1338.59) * mm});
            skPoint(sketch, "E448.0", {"position": v(-21576.39, 1250.88) * mm});
            skPoint(sketch, "E449.0", {"position": v(-22263.65, 1217.25) * mm});
            skPoint(sketch, "E450.0", {"position": v(-23022.43, 1235.2) * mm});
            skPoint(sketch, "E451.0", {"position": v(-22548.31, 5621.12) * mm});
            skPoint(sketch, "E452.0", {"position": v(-21396.82, 5619.96) * mm});
            skPoint(sketch, "E453.0", {"position": v(-24562.84, 5621.12) * mm});
            skPoint(sketch, "E454.0", {"position": v(-25629.98, -4455) * mm});
            skPoint(sketch, "E455.0", {"position": v(-26340.8, 5621.43) * mm});
            skPoint(sketch, "E456.0", {"position": v(-26340.8, 6095.06) * mm});
            skPoint(sketch, "E457.0", {"position": v(-20414.28, 6095.06) * mm});
            skPoint(sketch, "E458.0", {"position": v(-27289.16, -4573.46) * mm});
            skPoint(sketch, "E459.0", {"position": v(-27289.16, -4928.56) * mm});
            skPoint(sketch, "E460.0", {"position": v(-21955.54, -4928.56) * mm});
            skPoint(sketch, "E461.0", {"position": v(-21955.54, -4573.46) * mm});
            skPoint(sketch, "E462.0", {"position": v(-23615.09, -4573.15) * mm});
            skPoint(sketch, "E463.0", {"position": v(-23021.95, 880.03) * mm});
            skPoint(sketch, "E464.0", {"position": v(-27052.7, 6451.02) * mm});
            skLineSegment(sketch, "E465", {"start": v(-26340.8, 6095.06) * mm, "end": v(-20414.28, 6095.06) * mm});
            skLineSegment(sketch, "E466", {"start": v(-20414.28, 6095.06) * mm, "end": v(-19163.3, 5678.92) * mm});
            skLineSegment(sketch, "E467", {"start": v(-19163.3, 5678.92) * mm, "end": v(-18509.5, 5367.34) * mm});
            skLineSegment(sketch, "E468", {"start": v(-18509.5, 5367.34) * mm, "end": v(-17892.92, 4997.04) * mm});
            skLineSegment(sketch, "E469", {"start": v(-17892.92, 4997.04) * mm, "end": v(-17611.67, 4792.39) * mm});
            skLineSegment(sketch, "E470", {"start": v(-17611.67, 4792.39) * mm, "end": v(-17355.32, 4576.14) * mm});
            skLineSegment(sketch, "E471", {"start": v(-17355.32, 4576.14) * mm, "end": v(-17129.25, 4349.09) * mm});
            skLineSegment(sketch, "E472", {"start": v(-17129.25, 4349.09) * mm, "end": v(-16938.94, 4112.4) * mm});
            skLineSegment(sketch, "E473", {"start": v(-16938.94, 4112.4) * mm, "end": v(-16789.16, 3867.03) * mm});
            skLineSegment(sketch, "E474", {"start": v(-16789.16, 3867.03) * mm, "end": v(-16685.52, 3613.98) * mm});
            skLineSegment(sketch, "E475", {"start": v(-16685.52, 3613.98) * mm, "end": v(-16633.03, 3354.21) * mm});
            skLineSegment(sketch, "E476", {"start": v(-16633.03, 3354.21) * mm, "end": v(-16636.94, 3088.65) * mm});
            skLineSegment(sketch, "E477", {"start": v(-16636.94, 3088.65) * mm, "end": v(-16702.73, 2818.5) * mm});
            skLineSegment(sketch, "E478", {"start": v(-16702.73, 2818.5) * mm, "end": v(-16835.42, 2544.4) * mm});
            skLineSegment(sketch, "E479", {"start": v(-16835.42, 2544.4) * mm, "end": v(-17040.38, 2267.6) * mm});
            skLineSegment(sketch, "E480", {"start": v(-17040.38, 2267.6) * mm, "end": v(-17322.85, 1989.16) * mm});
            skLineSegment(sketch, "E481", {"start": v(-17322.85, 1989.16) * mm, "end": v(-17687.96, 1709.62) * mm});
            skLineSegment(sketch, "E482", {"start": v(-17687.96, 1709.62) * mm, "end": v(-20651.34, 879.97) * mm});
            skLineSegment(sketch, "E483", {"start": v(-20651.34, 879.97) * mm, "end": v(-20651.59, 761.07) * mm});
            skLineSegment(sketch, "E484", {"start": v(-20651.59, 761.07) * mm, "end": v(-20126.8, 640.84) * mm});
            skLineSegment(sketch, "E485", {"start": v(-20126.8, 640.84) * mm, "end": v(-19679.9, 487.03) * mm});
            skLineSegment(sketch, "E486", {"start": v(-19679.9, 487.03) * mm, "end": v(-19302.83, 301.3) * mm});
            skLineSegment(sketch, "E487", {"start": v(-19302.83, 301.3) * mm, "end": v(-18987.77, 85.78) * mm});
            skLineSegment(sketch, "E488", {"start": v(-18987.77, 85.78) * mm, "end": v(-18726.9, -157.26) * mm});
            skLineSegment(sketch, "E489", {"start": v(-18726.9, -157.26) * mm, "end": v(-18512.43, -425.88) * mm});
            skLineSegment(sketch, "E490", {"start": v(-18512.43, -425.88) * mm, "end": v(-18336.4, -718) * mm});
            skLineSegment(sketch, "E491", {"start": v(-18336.4, -718) * mm, "end": v(-18191.14, -1031.1) * mm});
            skLineSegment(sketch, "E492", {"start": v(-18191.14, -1031.1) * mm, "end": v(-17961.52, -1712.8) * mm});
            skLineSegment(sketch, "E493", {"start": v(-17961.52, -1712.8) * mm, "end": v(-17527.2, -3237.46) * mm});
            skLineSegment(sketch, "E494", {"start": v(-17527.2, -3237.46) * mm, "end": v(-17197.36, -4046.24) * mm});
            skLineSegment(sketch, "E495", {"start": v(-17197.36, -4046.24) * mm, "end": v(-16976.9, -4454.75) * mm});
            skLineSegment(sketch, "E496", {"start": v(-16976.9, -4454.75) * mm, "end": v(-14843, -4455) * mm});
            skLineSegment(sketch, "E497", {"start": v(-11158.54, -4581.58) * mm, "end": v(-10346.78, -4521.21) * mm});
            skLineSegment(sketch, "E498", {"start": v(-10346.78, -4521.21) * mm, "end": v(-9598.85, -4393.53) * mm});
            skLineSegment(sketch, "E499", {"start": v(-9598.85, -4393.53) * mm, "end": v(-9260.35, -4298.56) * mm});
            skLineSegment(sketch, "E500", {"start": v(-9260.35, -4298.56) * mm, "end": v(-8951.63, -4179.9) * mm});
            skLineSegment(sketch, "E501", {"start": v(-8951.63, -4179.9) * mm, "end": v(-8677.22, -4035.25) * mm});
            skLineSegment(sketch, "E502", {"start": v(-8677.22, -4035.25) * mm, "end": v(-8441.62, -3862.34) * mm});
            skLineSegment(sketch, "E503", {"start": v(-8441.62, -3862.34) * mm, "end": v(-8203.34, -3602.57) * mm});
            skLineSegment(sketch, "E504", {"start": v(-8203.34, -3602.57) * mm, "end": v(-7979.71, -3259.56) * mm});
            skLineSegment(sketch, "E505", {"start": v(-7979.71, -3259.56) * mm, "end": v(-7772.8, -2843.3) * mm});
            skLineSegment(sketch, "E506", {"start": v(-7772.8, -2843.3) * mm, "end": v(-7417.7, -1832.74) * mm});
            skLineSegment(sketch, "E507", {"start": v(-7417.7, -1832.74) * mm, "end": v(-7154.27, -653.66) * mm});
            skLineSegment(sketch, "E508", {"start": v(-7154.27, -653.66) * mm, "end": v(-6999.12, 611.11) * mm});
            skLineSegment(sketch, "E509", {"start": v(-6999.12, 611.11) * mm, "end": v(-6968.97, 1878.93) * mm});
            skLineSegment(sketch, "E510", {"start": v(-6968.97, 1878.93) * mm, "end": v(-7080.17, 3067.29) * mm});
            skLineSegment(sketch, "E511", {"start": v(-7080.17, 3067.29) * mm, "end": v(-7194.07, 3605.74) * mm});
            skLineSegment(sketch, "E512", {"start": v(-7194.07, 3605.74) * mm, "end": v(-7349.46, 4093.29) * mm});
            skLineSegment(sketch, "E513", {"start": v(-7349.46, 4093.29) * mm, "end": v(-7548.44, 4519.74) * mm});
            skLineSegment(sketch, "E514", {"start": v(-7548.44, 4519.74) * mm, "end": v(-7793.43, 4874.42) * mm});
            skLineSegment(sketch, "E515", {"start": v(-7793.43, 4874.42) * mm, "end": v(-8085.91, 5147.37) * mm});
            skLineSegment(sketch, "E516", {"start": v(-8085.91, 5147.37) * mm, "end": v(-8316.5, 5286.16) * mm});
            skLineSegment(sketch, "E517", {"start": v(-8316.5, 5286.16) * mm, "end": v(-8580.3, 5397.85) * mm});
            skLineSegment(sketch, "E518", {"start": v(-8580.3, 5397.85) * mm, "end": v(-8872.65, 5485.01) * mm});
            skLineSegment(sketch, "E519", {"start": v(-8047.22, 5704.98) * mm, "end": v(-7770.12, 5621.55) * mm});
            skLineSegment(sketch, "E520", {"start": v(-7770.12, 5621.55) * mm, "end": v(-7505.96, 5516.14) * mm});
            skLineSegment(sketch, "E521", {"start": v(-7505.96, 5516.14) * mm, "end": v(-7256.57, 5383.75) * mm});
            skLineSegment(sketch, "E522", {"start": v(-7256.57, 5383.75) * mm, "end": v(-6807.35, 5067.35) * mm});
            skLineSegment(sketch, "E523", {"start": v(-6807.35, 5067.35) * mm, "end": v(-6407.69, 4700.53) * mm});
            skLineSegment(sketch, "E524", {"start": v(-8872.65, 5485.01) * mm, "end": v(-9527.68, 5596.83) * mm});
            skLineSegment(sketch, "E525", {"start": v(-9527.68, 5596.83) * mm, "end": v(-10249.24, 5642.54) * mm});
            skLineSegment(sketch, "E526", {"start": v(-10249.24, 5642.54) * mm, "end": v(-11760.96, 5621.43) * mm});
            skLineSegment(sketch, "E527", {"start": v(-11760.96, 5621.43) * mm, "end": v(-12235.45, 1116.67) * mm});
            skLineSegment(sketch, "E528", {"start": v(-12235.45, 1116.67) * mm, "end": v(-10694.55, 997.83) * mm});
            skLineSegment(sketch, "E529", {"start": v(-10694.55, 997.83) * mm, "end": v(-10812.72, 761.44) * mm});
            skLineSegment(sketch, "E530", {"start": v(-10812.72, 761.44) * mm, "end": v(-12353.49, 642.79) * mm});
            skLineSegment(sketch, "E531", {"start": v(-12353.49, 642.79) * mm, "end": v(-12828.1, -4573.15) * mm});
            skLineSegment(sketch, "E532", {"start": v(-12828.1, -4573.15) * mm, "end": v(-11158.54, -4581.58) * mm});
            skLineSegment(sketch, "E533", {"start": v(-15553.8, 6095.06) * mm, "end": v(-10219.82, 6095.06) * mm});
            skLineSegment(sketch, "E534", {"start": v(-10219.82, 6095.06) * mm, "end": v(-8047.22, 5704.98) * mm});
            skLineSegment(sketch, "E535", {"start": v(-15553.8, 6095.06) * mm, "end": v(-15553.8, 5621.43) * mm});
            skLineSegment(sketch, "E536", {"start": v(-15553.8, 5621.43) * mm, "end": v(-13775.73, 5621.12) * mm});
            skLineSegment(sketch, "E537", {"start": v(-13775.73, 5621.12) * mm, "end": v(-14250.22, 1116.36) * mm});
            skLineSegment(sketch, "E538", {"start": v(-14250.22, 1116.36) * mm, "end": v(-14922.34, 1107.2) * mm});
            skLineSegment(sketch, "E539", {"start": v(-14922.34, 1107.2) * mm, "end": v(-15104.47, 1079.98) * mm});
            skLineSegment(sketch, "E540", {"start": v(-15269.02, 1035.3) * mm, "end": v(-15104.47, 1079.98) * mm});
            skLineSegment(sketch, "E541", {"start": v(-15269.02, 1035.3) * mm, "end": v(-15418.19, 969.45) * mm});
            skLineSegment(sketch, "E542", {"start": v(-15553.8, 879.42) * mm, "end": v(-15418.19, 969.45) * mm});
            skLineSegment(sketch, "E543", {"start": v(-15553.8, 761.44) * mm, "end": v(-15553.8, 879.42) * mm});
            skLineSegment(sketch, "E544", {"start": v(-15553.8, 761.44) * mm, "end": v(-14368.38, 761.07) * mm});
            skLineSegment(sketch, "E545", {"start": v(-14368.38, 761.07) * mm, "end": v(-14843, -4455) * mm});
            skLineSegment(sketch, "E546", {"start": v(-6407.69, 4700.53) * mm, "end": v(-6057.35, 4288.66) * mm});
            skLineSegment(sketch, "E547", {"start": v(-6057.35, 4288.66) * mm, "end": v(-5756.32, 3837.12) * mm});
            skLineSegment(sketch, "E548", {"start": v(-5504.61, 3351.65) * mm, "end": v(-5756.32, 3837.12) * mm});
            skLineSegment(sketch, "E549", {"start": v(-5302.1, 2837.37) * mm, "end": v(-5504.61, 3351.65) * mm});
            skLineSegment(sketch, "E550", {"start": v(-5148.78, 2299.95) * mm, "end": v(-5302.1, 2837.37) * mm});
            skLineSegment(sketch, "E551", {"start": v(-5044.65, 1744.6) * mm, "end": v(-5148.78, 2299.95) * mm});
            skLineSegment(sketch, "E552", {"start": v(-4989.48, 1177.27) * mm, "end": v(-5044.65, 1744.6) * mm});
            skLineSegment(sketch, "E553", {"start": v(-4983.37, 602.87) * mm, "end": v(-4989.48, 1177.27) * mm});
            skLineSegment(sketch, "E554", {"start": v(-5026.34, 27.19) * mm, "end": v(-4983.37, 602.87) * mm});
            skLineSegment(sketch, "E555", {"start": v(-5118.02, -544.53) * mm, "end": v(-5026.34, 27.19) * mm});
            skLineSegment(sketch, "E556", {"start": v(-5258.64, -1106.54) * mm, "end": v(-5118.02, -544.53) * mm});
            skLineSegment(sketch, "E557", {"start": v(-5447.97, -1653.6) * mm, "end": v(-5258.64, -1106.54) * mm});
            skLineSegment(sketch, "E558", {"start": v(-5686.13, -2180.2) * mm, "end": v(-5447.97, -1653.6) * mm});
            skLineSegment(sketch, "E559", {"start": v(-5973, -2681.06) * mm, "end": v(-5686.13, -2180.2) * mm});
            skLineSegment(sketch, "E560", {"start": v(-6308.45, -3150.49) * mm, "end": v(-5973, -2681.06) * mm});
            skLineSegment(sketch, "E561", {"start": v(-6604.1, -3478.43) * mm, "end": v(-6308.45, -3150.49) * mm});
            skLineSegment(sketch, "E562", {"start": v(-6932.1, -3763.64) * mm, "end": v(-6604.1, -3478.43) * mm});
            skLineSegment(sketch, "E563", {"start": v(-7291.23, -4008.58) * mm, "end": v(-6932.1, -3763.64) * mm});
            skLineSegment(sketch, "E564", {"start": v(-7680.03, -4216.83) * mm, "end": v(-7291.23, -4008.58) * mm});
            skLineSegment(sketch, "E565", {"start": v(-8096.65, -4391.09) * mm, "end": v(-7680.03, -4216.83) * mm});
            skLineSegment(sketch, "E566", {"start": v(-8540.38, -4534.46) * mm, "end": v(-8096.65, -4391.09) * mm});
            skLineSegment(sketch, "E567", {"start": v(-9502.05, -4740.33) * mm, "end": v(-8540.38, -4534.46) * mm});
            skLineSegment(sketch, "E568", {"start": v(-10553.32, -4858.68) * mm, "end": v(-9502.05, -4740.33) * mm});
            skLineSegment(sketch, "E569", {"start": v(-10553.32, -4858.68) * mm, "end": v(-17687.84, -5047.1) * mm});
            skLineSegment(sketch, "E570", {"start": v(-17687.84, -5047.1) * mm, "end": v(-18153.05, -4900.6) * mm});
            skLineSegment(sketch, "E571", {"start": v(-18153.05, -4900.6) * mm, "end": v(-18535.37, -4695.83) * mm});
            skLineSegment(sketch, "E572", {"start": v(-19435.76, -3435.95) * mm, "end": v(-19285, -3802.7) * mm});
            skLineSegment(sketch, "E573", {"start": v(-19091.28, -4139.8) * mm, "end": v(-19285, -3802.7) * mm});
            skLineSegment(sketch, "E574", {"start": v(-18844.94, -4439.91) * mm, "end": v(-19091.28, -4139.8) * mm});
            skLineSegment(sketch, "E575", {"start": v(-18535.37, -4695.83) * mm, "end": v(-18844.94, -4439.91) * mm});
            skLineSegment(sketch, "E576", {"start": v(-19435.76, -3435.95) * mm, "end": v(-19648.78, -2641.33) * mm});
            skLineSegment(sketch, "E577", {"start": v(-20000.1, -1008.7) * mm, "end": v(-19648.78, -2641.33) * mm});
            skLineSegment(sketch, "E578", {"start": v(-21125.22, 524.26) * mm, "end": v(-20785.86, 300.87) * mm});
            skLineSegment(sketch, "E579", {"start": v(-20785.86, 300.87) * mm, "end": v(-20513.65, 28.77) * mm});
            skLineSegment(sketch, "E580", {"start": v(-20513.65, 28.77) * mm, "end": v(-20298.56, -285.07) * mm});
            skLineSegment(sketch, "E581", {"start": v(-20298.56, -285.07) * mm, "end": v(-20130.83, -633.15) * mm});
            skLineSegment(sketch, "E582", {"start": v(-20130.83, -633.15) * mm, "end": v(-20000.1, -1008.7) * mm});
            skLineSegment(sketch, "E583", {"start": v(-26340.8, 6095.06) * mm, "end": v(-26340.8, 5621.43) * mm});
            skLineSegment(sketch, "E584", {"start": v(-26340.8, 5621.43) * mm, "end": v(-24562.84, 5621.12) * mm});
            skLineSegment(sketch, "E585", {"start": v(-24562.84, 5621.12) * mm, "end": v(-25629.98, -4455) * mm});
            skLineSegment(sketch, "E586", {"start": v(-25629.98, -4455) * mm, "end": v(-27289.16, -4573.46) * mm});
            skLineSegment(sketch, "E587", {"start": v(-27289.16, -4573.46) * mm, "end": v(-27289.16, -4928.56) * mm});
            skLineSegment(sketch, "E588", {"start": v(-27289.16, -4928.56) * mm, "end": v(-21955.54, -4928.56) * mm});
            skLineSegment(sketch, "E589", {"start": v(-21955.54, -4928.56) * mm, "end": v(-21955.54, -4573.46) * mm});
            skLineSegment(sketch, "E590", {"start": v(-21955.54, -4573.46) * mm, "end": v(-23615.09, -4573.15) * mm});
            skLineSegment(sketch, "E591", {"start": v(-23615.09, -4573.15) * mm, "end": v(-23021.95, 880.03) * mm});
            skLineSegment(sketch, "E592", {"start": v(-23021.95, 880.03) * mm, "end": v(-21125.22, 524.26) * mm});
            skLineSegment(sketch, "E593", {"start": v(-23022.43, 1235.2) * mm, "end": v(-22263.65, 1217.25) * mm});
            skLineSegment(sketch, "E594", {"start": v(-22263.65, 1217.25) * mm, "end": v(-21576.39, 1250.88) * mm});
            skLineSegment(sketch, "E595", {"start": v(-21576.39, 1250.88) * mm, "end": v(-20962.38, 1338.59) * mm});
            skLineSegment(sketch, "E596", {"start": v(-20962.38, 1338.59) * mm, "end": v(-20423.92, 1483.24) * mm});
            skLineSegment(sketch, "E597", {"start": v(-23022.43, 1235.2) * mm, "end": v(-22548.31, 5621.12) * mm});
            skLineSegment(sketch, "E598", {"start": v(-22548.31, 5621.12) * mm, "end": v(-21396.82, 5619.96) * mm});
            skLineSegment(sketch, "E599", {"start": v(-21396.82, 5619.96) * mm, "end": v(-19853, 5384.85) * mm});
            skLineSegment(sketch, "E600", {"start": v(-19853, 5384.85) * mm, "end": v(-19592.01, 5287.44) * mm});
            skLineSegment(sketch, "E601", {"start": v(-19592.01, 5287.44) * mm, "end": v(-19344.58, 5169.34) * mm});
            skLineSegment(sketch, "E602", {"start": v(-19344.58, 5169.34) * mm, "end": v(-19109.96, 5028.6) * mm});
            skLineSegment(sketch, "E603", {"start": v(-19109.96, 5028.6) * mm, "end": v(-18962.25, 4326.87) * mm});
            skLineSegment(sketch, "E604", {"start": v(-20423.92, 1483.24) * mm, "end": v(-19963.6, 1687.65) * mm});
            skLineSegment(sketch, "E605", {"start": v(-19963.6, 1687.65) * mm, "end": v(-19583.23, 1954.56) * mm});
            skLineSegment(sketch, "E606", {"start": v(-19583.23, 1954.56) * mm, "end": v(-19285.25, 2287.01) * mm});
            skLineSegment(sketch, "E607", {"start": v(-19285.25, 2287.01) * mm, "end": v(-19071.87, 2687.59) * mm});
            skLineSegment(sketch, "E608", {"start": v(-19071.87, 2687.59) * mm, "end": v(-18945.53, 3159.27) * mm});
            skLineSegment(sketch, "E609", {"start": v(-18945.53, 3159.27) * mm, "end": v(-18908.18, 3704.74) * mm});
            skLineSegment(sketch, "E610", {"start": v(-18962.25, 4326.87) * mm, "end": v(-18908.18, 3704.74) * mm});
            skSolve(sketch);
        }
        {
            var Q0;
            Q0 = qSketchRegion(id + "F0", true);
            extrude(context, id + "F1", {"entities" : qUnion([Q0]), "depth" : 1000 * mm});
        }
    });
